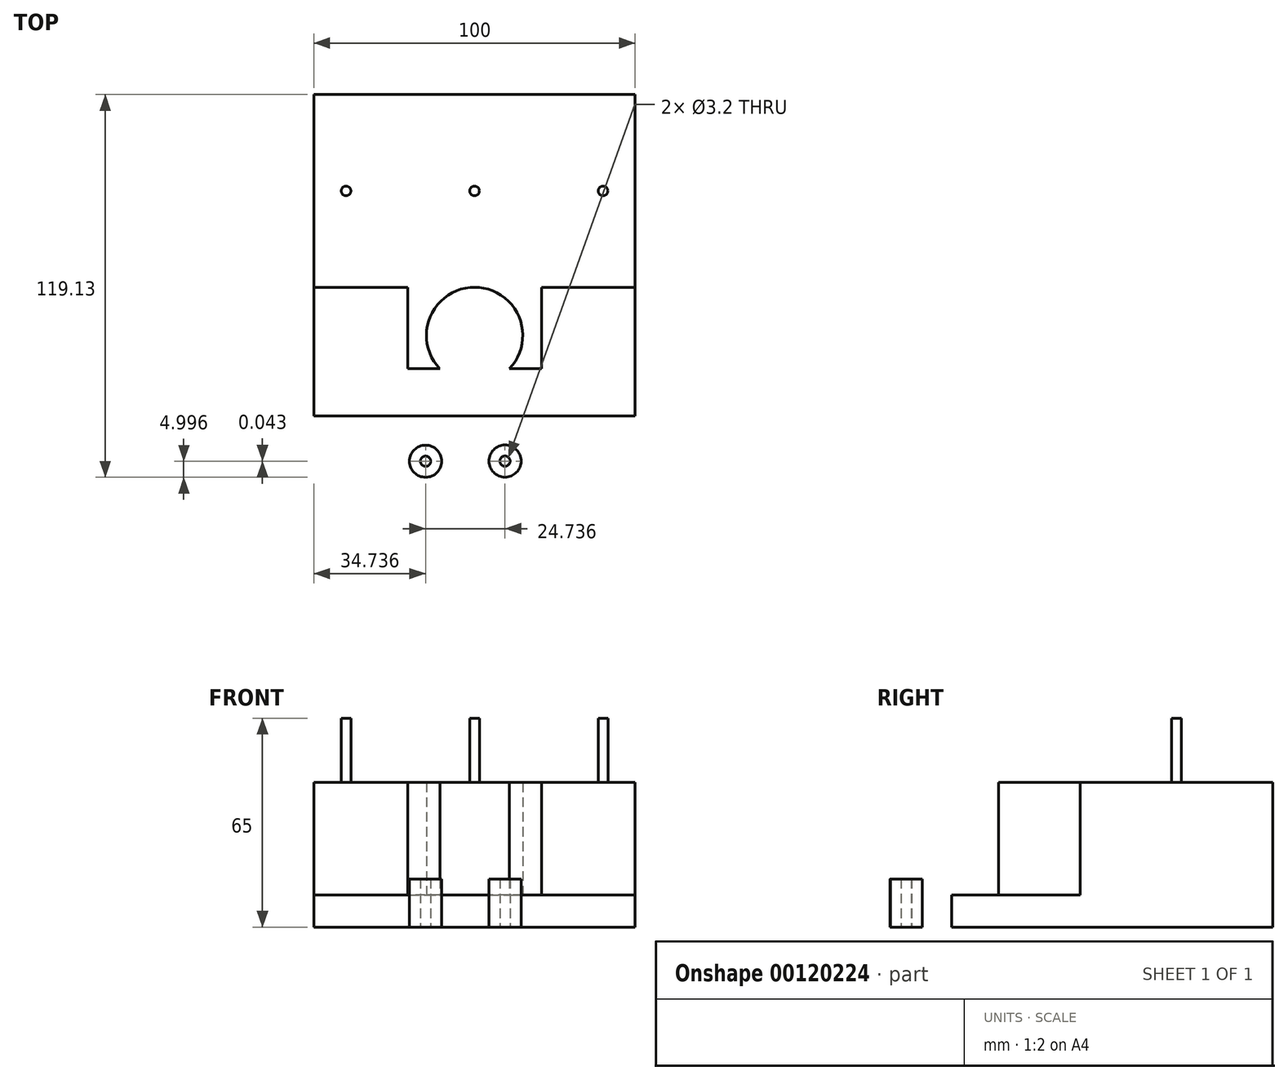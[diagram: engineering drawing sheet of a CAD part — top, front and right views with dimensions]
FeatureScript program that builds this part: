
annotation { "Feature Type Name" : "Feature", "Feature Type Description" : "" }
export const myFeature = defineFeature(function(context is Context, id is Id, definition is map)
    precondition{}
    {
        {
            var Q0;
            Q0=qCreatedBy(makeId("Top.planeOp"),FACE);
            var sketch = newSketch(context, id + "F0", { "sketchPlane" : qUnion([Q0])});
            skLineSegment(sketch, "E0.bottom", {"start": v(-43.03, 68.67) * mm, "end": v(56.97, 68.67) * mm});
            skLineSegment(sketch, "E0.top", {"start": v(-43.03, -31.33) * mm, "end": v(56.97, -31.33) * mm});
            skLineSegment(sketch, "E0.left", {"start": v(-43.03, 68.67) * mm, "end": v(-43.03, -31.33) * mm});
            skLineSegment(sketch, "E0.right", {"start": v(56.97, 68.67) * mm, "end": v(56.97, -31.33) * mm});
            skCircle(sketch, "E1", {"center": v(-8.3, -45.46) * mm, "radius": 1.6 * mm});
            skCircle(sketch, "E2", {"center": v(-8.3, -45.46) * mm, "radius": 5 * mm});
            skCircle(sketch, "E3", {"center": v(16.44, -45.42) * mm, "radius": 1.6 * mm});
            skCircle(sketch, "E4", {"center": v(16.44, -45.42) * mm, "radius": 5 * mm});
            skSolve(sketch);
        }
        {
            var Q0;
            Q0=makeQuery(id+"F0.imprint","IMPRINT",FACE,{"disambiguationData":[TD([[makeQuery(id+"F0.imprint","IMPRINT",EDGE,{"derivedFrom":sQuery(id+"F0.wireOp",EDGE,"E0.bottom")}),-1.0]])]});
            extrude(context, id + "F1", {"entities" : qUnion([Q0]), "depth" : 10 * mm});
        }
        {
            var Q0;
            Q0=makeQuery(id+"F1.opExtrude","CAP_FACE",FACE,{"disambiguationData":[OSD([sQuery(id+"F0.wireOp",EDGE,"E0.bottom"),sQuery(id+"F0.wireOp",EDGE,"E0.top"),sQuery(id+"F0.wireOp",EDGE,"E0.left"),sQuery(id+"F0.wireOp",EDGE,"E0.right")])],"isStart":false});
            var sketch = newSketch(context, id + "F2", { "sketchPlane" : qUnion([Q0])});
            skLineSegment(sketch, "E5.bottom", {"start": v(-43.03, 68.67) * mm, "end": v(56.97, 68.67) * mm});
            skLineSegment(sketch, "E5.top", {"start": v(-43.03, 8.67) * mm, "end": v(56.97, 8.67) * mm});
            skLineSegment(sketch, "E5.left", {"start": v(-43.03, 68.67) * mm, "end": v(-43.03, 8.67) * mm});
            skLineSegment(sketch, "E5.right", {"start": v(56.97, 68.67) * mm, "end": v(56.97, 8.67) * mm});
            skLineSegment(sketch, "E6", {"start": v(6.97, 8.67) * mm, "end": v(6.97, -6.33) * mm});
            skCircle(sketch, "E7", {"center": v(6.97, -6.33) * mm, "radius": 15 * mm});
            skLineSegment(sketch, "E8", {"start": v(-3.86, -16.7) * mm, "end": v(17.8, -16.7) * mm});
            skLineSegment(sketch, "E9", {"start": v(17.8, -16.7) * mm, "end": v(27.8, -16.7) * mm});
            skLineSegment(sketch, "E10", {"start": v(-3.86, -16.7) * mm, "end": v(-13.86, -16.7) * mm});
            skLineSegment(sketch, "E11", {"start": v(27.8, -16.7) * mm, "end": v(27.8, 8.67) * mm});
            skLineSegment(sketch, "E12", {"start": v(-13.86, -16.7) * mm, "end": v(-13.86, 8.67) * mm});
            skSolve(sketch);
        }
        {
            var Q0;
            Q0=makeQuery(id+"F2.imprint","IMPRINT",FACE,{"disambiguationData":[TD([[makeQuery(id+"F2.imprint","IMPRINT",EDGE,{"derivedFrom":sQuery(id+"F2.wireOp",EDGE,"E5.bottom")}),-1.0]])]});
            var Q1;
            {var subQ4=sQuery(id+"F2.wireOp",EDGE,"E10");Q1=makeQuery(id+"F2.imprint","IMPRINT",FACE,{"disambiguationData":[TD([[makeQuery(id+"F2.imprint","IMPRINT",EDGE,{"derivedFrom":subQ4}),-1.0]])]});}
            var Q2;
            {var subQ4=sQuery(id+"F2.wireOp",EDGE,"E9");Q2=makeQuery(id+"F2.imprint","IMPRINT",FACE,{"disambiguationData":[TD([[makeQuery(id+"F2.imprint","IMPRINT",EDGE,{"derivedFrom":subQ4}),1.0]])]});}
            extrude(context, id + "F3", {"entities" : qUnion([Q0, Q1, Q2]), "operationType" : NewBodyOperationType.ADD, "depth" : 35 * mm});
        }
        {
            var Q0;
            Q0=makeQuery(id+"F3.opExtrude","CAP_FACE",FACE,{"disambiguationData":[OSD([sQuery(id+"F2.wireOp",EDGE,"E5.bottom"),sQuery(id+"F2.wireOp",EDGE,"E5.top"),sQuery(id+"F2.wireOp",EDGE,"E5.left"),sQuery(id+"F2.wireOp",EDGE,"E5.right")])],"isStart":false});
            var sketch = newSketch(context, id + "F4", { "sketchPlane" : qUnion([Q0])});
            skCircle(sketch, "E13", {"center": v(6.97, 38.67) * mm, "radius": 1.5 * mm});
            skCircle(sketch, "E14", {"center": v(-33.03, 38.67) * mm, "radius": 1.5 * mm});
            skCircle(sketch, "E15", {"center": v(46.97, 38.67) * mm, "radius": 1.5 * mm});
            skSolve(sketch);
        }
        {
            var Q0;
            Q0=makeQuery(id+"F4.imprint","IMPRINT",FACE,{"disambiguationData":[TD([[makeQuery(id+"F4.imprint","IMPRINT",EDGE,{"derivedFrom":sQuery(id+"F4.wireOp",EDGE,"E14")}),1.0]])]});
            var Q1;
            Q1=makeQuery(id+"F4.imprint","IMPRINT",FACE,{"disambiguationData":[TD([[makeQuery(id+"F4.imprint","IMPRINT",EDGE,{"derivedFrom":sQuery(id+"F4.wireOp",EDGE,"E13")}),1.0]])]});
            var Q2;
            Q2=makeQuery(id+"F4.imprint","IMPRINT",FACE,{"disambiguationData":[TD([[makeQuery(id+"F4.imprint","IMPRINT",EDGE,{"derivedFrom":sQuery(id+"F4.wireOp",EDGE,"E15")}),1.0]])]});
            extrude(context, id + "F5", {"entities" : qUnion([Q0, Q1, Q2]), "operationType" : NewBodyOperationType.ADD, "depth" : 20 * mm});
        }
        {
            var Q0;
            Q0=makeQuery(id+"F0.imprint","IMPRINT",FACE,{"disambiguationData":[TD([[makeQuery(id+"F0.imprint","IMPRINT",EDGE,{"derivedFrom":sQuery(id+"F0.wireOp",EDGE,"E1")}),-1.0]])]});
            var Q1;
            Q1=makeQuery(id+"F0.imprint","IMPRINT",FACE,{"disambiguationData":[TD([[makeQuery(id+"F0.imprint","IMPRINT",EDGE,{"derivedFrom":sQuery(id+"F0.wireOp",EDGE,"E3")}),-1.0]])]});
            extrude(context, id + "F6", {"entities" : qUnion([Q0, Q1]), "depth" : 15 * mm});
        }
    });
